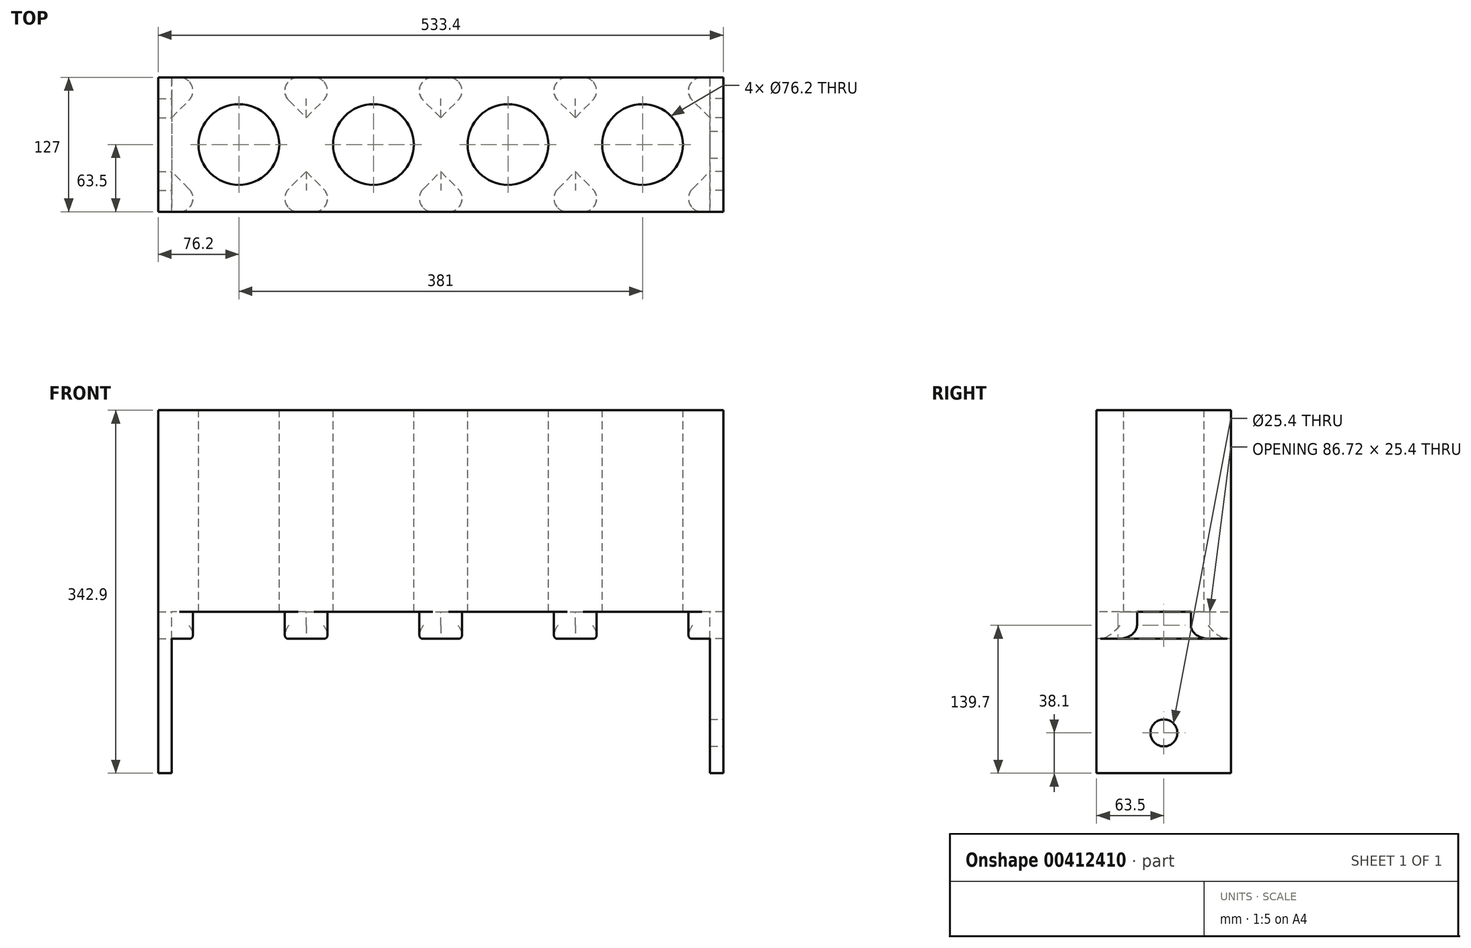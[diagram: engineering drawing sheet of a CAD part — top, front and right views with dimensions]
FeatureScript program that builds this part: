
annotation { "Feature Type Name" : "Feature", "Feature Type Description" : "" }
export const myFeature = defineFeature(function(context is Context, id is Id, definition is map)
    precondition{}
    {
        {
            var Q0;
            Q0=qCreatedBy(makeId("Top.planeOp"),FACE);
            var sketch = newSketch(context, id + "F0", { "sketchPlane" : qUnion([Q0])});
            skLineSegment(sketch, "E0", {"start": v(508, 0) * mm, "end": v(0, 0) * mm});
            skLineSegment(sketch, "E1", {"start": v(0, 0) * mm, "end": v(0, 127) * mm});
            skLineSegment(sketch, "E2", {"start": v(0, 127) * mm, "end": v(508, 127) * mm});
            skLineSegment(sketch, "E3", {"start": v(508, 0) * mm, "end": v(508, 127) * mm});
            skCircle(sketch, "E4", {"center": v(63.5, 63.5) * mm, "radius": 38.1 * mm});
            skCircle(sketch, "E5", {"center": v(190.5, 63.5) * mm, "radius": 38.1 * mm});
            skCircle(sketch, "E6", {"center": v(317.5, 63.5) * mm, "radius": 38.1 * mm});
            skCircle(sketch, "E7", {"center": v(444.5, 63.5) * mm, "radius": 38.1 * mm});
            skSolve(sketch);
        }
        {
            var Q0;
            Q0 = qSketchRegion(id + "F0", true);
            extrude(context, id + "F1", {"entities" : qUnion([Q0]), "oppositeDirection" : true, "depth" : 190.5 * mm});
        }
        {
            var Q0;
            Q0=makeQuery(id+"F1.opExtrude","CAP_FACE",FACE,{"disambiguationData":[OSD([sQuery(id+"F0.wireOp",EDGE,"E0"),sQuery(id+"F0.wireOp",EDGE,"E1"),sQuery(id+"F0.wireOp",EDGE,"E2"),sQuery(id+"F0.wireOp",EDGE,"E3"),sQuery(id+"F0.wireOp",EDGE,"E4"),sQuery(id+"F0.wireOp",EDGE,"E5"),sQuery(id+"F0.wireOp",EDGE,"E6"),sQuery(id+"F0.wireOp",EDGE,"E7")])],"isStart":false});
            var sketch = newSketch(context, id + "F2", { "sketchPlane" : qUnion([Q0])});
            skLineSegment(sketch, "E8", {"start": v(38.1, 0) * mm, "end": v(0, -38.1) * mm});
            skLineSegment(sketch, "E9", {"start": v(0, -88.9) * mm, "end": v(38.1, -127) * mm});
            skLineSegment(sketch, "E10", {"start": v(127, 0) * mm, "end": v(127, -38.1) * mm});
            skLineSegment(sketch, "E11", {"start": v(254, 0) * mm, "end": v(254, -127) * mm});
            skLineSegment(sketch, "E12", {"start": v(381, 0) * mm, "end": v(381, -127) * mm});
            skLineSegment(sketch, "E13", {"start": v(127, -38.1) * mm, "end": v(88.9, 0) * mm});
            skLineSegment(sketch, "E14", {"start": v(88.9, -127) * mm, "end": v(127, -88.9) * mm});
            skLineSegment(sketch, "E15", {"start": v(127, -38.1) * mm, "end": v(165.1, 0) * mm});
            skLineSegment(sketch, "E16", {"start": v(127, -88.9) * mm, "end": v(165.1, -127) * mm});
            skLineSegment(sketch, "E17", {"start": v(254, -88.9) * mm, "end": v(215.9, -127) * mm});
            skLineSegment(sketch, "E18", {"start": v(254, -88.9) * mm, "end": v(292.1, -127) * mm});
            skLineSegment(sketch, "E19", {"start": v(215.9, 0) * mm, "end": v(254, -38.1) * mm});
            skLineSegment(sketch, "E20", {"start": v(254, -38.1) * mm, "end": v(292.1, 0) * mm});
            skLineSegment(sketch, "E21", {"start": v(342.9, 0) * mm, "end": v(381, -38.1) * mm});
            skLineSegment(sketch, "E22", {"start": v(381, -38.1) * mm, "end": v(419.1, 0) * mm});
            skLineSegment(sketch, "E23", {"start": v(381, -88.9) * mm, "end": v(342.9, -127) * mm});
            skLineSegment(sketch, "E24", {"start": v(381, -88.9) * mm, "end": v(419.1, -127) * mm});
            skLineSegment(sketch, "E25", {"start": v(469.9, 0) * mm, "end": v(508, -38.1) * mm});
            skLineSegment(sketch, "E26", {"start": v(508, -88.9) * mm, "end": v(469.9, -127) * mm});
            skLineSegment(sketch, "E27.trimOffspring", {"start": v(127, -88.9) * mm, "end": v(127, -127) * mm});
            skSolve(sketch);
        }
        {
            var Q0;
            {var subQ3=sQuery(id+"F2.wireOp",EDGE,"E19");Q0=makeQuery(id+"F2.imprint","IMPRINT",FACE,{"disambiguationData":[TD([[makeQuery(id+"F2.imprint","IMPRINT",EDGE,{"derivedFrom":subQ3}),1.0]])]});}
            var Q1;
            {var subQ3=sQuery(id+"F2.wireOp",EDGE,"E20");Q1=makeQuery(id+"F2.imprint","IMPRINT",FACE,{"disambiguationData":[TD([[makeQuery(id+"F2.imprint","IMPRINT",EDGE,{"derivedFrom":subQ3}),1.0]])]});}
            var Q2;
            {var subQ3=sQuery(id+"F2.wireOp",EDGE,"E17");Q2=makeQuery(id+"F2.imprint","IMPRINT",FACE,{"disambiguationData":[TD([[makeQuery(id+"F2.imprint","IMPRINT",EDGE,{"derivedFrom":subQ3}),1.0]])]});}
            var Q3;
            {var subQ3=sQuery(id+"F2.wireOp",EDGE,"E18");Q3=makeQuery(id+"F2.imprint","IMPRINT",FACE,{"disambiguationData":[TD([[makeQuery(id+"F2.imprint","IMPRINT",EDGE,{"derivedFrom":subQ3}),-1.0]])]});}
            var Q4;
            {var subQ0=sQuery(id+"F2.wireOp",EDGE,"E10");Q4=makeQuery(id+"F2.imprint","IMPRINT",FACE,{"disambiguationData":[TD([[makeQuery(id+"F2.imprint","IMPRINT",EDGE,{"derivedFrom":subQ0}),1.0]])]});}
            var Q5;
            {var subQ0=sQuery(id+"F2.wireOp",EDGE,"E10");Q5=makeQuery(id+"F2.imprint","IMPRINT",FACE,{"disambiguationData":[TD([[makeQuery(id+"F2.imprint","IMPRINT",EDGE,{"derivedFrom":subQ0}),-1.0]])]});}
            var Q6;
            {var subQ0=sQuery(id+"F2.wireOp",EDGE,"E14");Q6=makeQuery(id+"F2.imprint","IMPRINT",FACE,{"disambiguationData":[TD([[makeQuery(id+"F2.imprint","IMPRINT",EDGE,{"derivedFrom":subQ0}),-1.0]])]});}
            var Q7;
            {var subQ0=sQuery(id+"F2.wireOp",EDGE,"E16");Q7=makeQuery(id+"F2.imprint","IMPRINT",FACE,{"disambiguationData":[TD([[makeQuery(id+"F2.imprint","IMPRINT",EDGE,{"derivedFrom":subQ0}),-1.0]])]});}
            var Q8;
            {var subQ0=sQuery(id+"F2.wireOp",EDGE,"E8");Q8=makeQuery(id+"F2.imprint","IMPRINT",FACE,{"disambiguationData":[TD([[makeQuery(id+"F2.imprint","IMPRINT",EDGE,{"derivedFrom":subQ0}),-1.0]])]});}
            var Q9;
            {var subQ0=sQuery(id+"F2.wireOp",EDGE,"E9");Q9=makeQuery(id+"F2.imprint","IMPRINT",FACE,{"disambiguationData":[TD([[makeQuery(id+"F2.imprint","IMPRINT",EDGE,{"derivedFrom":subQ0}),-1.0]])]});}
            var Q10;
            {var subQ3=sQuery(id+"F2.wireOp",EDGE,"E21");Q10=makeQuery(id+"F2.imprint","IMPRINT",FACE,{"disambiguationData":[TD([[makeQuery(id+"F2.imprint","IMPRINT",EDGE,{"derivedFrom":subQ3}),1.0]])]});}
            var Q11;
            {var subQ3=sQuery(id+"F2.wireOp",EDGE,"E22");Q11=makeQuery(id+"F2.imprint","IMPRINT",FACE,{"disambiguationData":[TD([[makeQuery(id+"F2.imprint","IMPRINT",EDGE,{"derivedFrom":subQ3}),1.0]])]});}
            var Q12;
            {var subQ0=sQuery(id+"F2.wireOp",EDGE,"E25");Q12=makeQuery(id+"F2.imprint","IMPRINT",FACE,{"disambiguationData":[TD([[makeQuery(id+"F2.imprint","IMPRINT",EDGE,{"derivedFrom":subQ0}),1.0]])]});}
            var Q13;
            {var subQ0=sQuery(id+"F2.wireOp",EDGE,"E26");Q13=makeQuery(id+"F2.imprint","IMPRINT",FACE,{"disambiguationData":[TD([[makeQuery(id+"F2.imprint","IMPRINT",EDGE,{"derivedFrom":subQ0}),1.0]])]});}
            var Q14;
            {var subQ3=sQuery(id+"F2.wireOp",EDGE,"E23");Q14=makeQuery(id+"F2.imprint","IMPRINT",FACE,{"disambiguationData":[TD([[makeQuery(id+"F2.imprint","IMPRINT",EDGE,{"derivedFrom":subQ3}),1.0]])]});}
            var Q15;
            {var subQ3=sQuery(id+"F2.wireOp",EDGE,"E24");Q15=makeQuery(id+"F2.imprint","IMPRINT",FACE,{"disambiguationData":[TD([[makeQuery(id+"F2.imprint","IMPRINT",EDGE,{"derivedFrom":subQ3}),-1.0]])]});}
            extrude(context, id + "F3", {"entities" : qUnion([Q0, Q1, Q2, Q3, Q4, Q5, Q6, Q7, Q8, Q9, Q10, Q11, Q12, Q13, Q14, Q15]), "operationType" : NewBodyOperationType.ADD, "depth" : 25.4 * mm});
        }
        {
            var Q0;
            Q0=makeQuery(id+"F3.opExtrude","CAP_EDGE",EDGE,{"disambiguationData":[OSD([sQuery(id+"F2.wireOp",EDGE,"E22")])],"isStart":false});
            var Q1;
            Q1=makeQuery(id+"F3.opExtrude","CAP_EDGE",EDGE,{"disambiguationData":[OSD([sQuery(id+"F2.wireOp",EDGE,"E21")])],"isStart":false});
            var Q2;
            Q2=makeQuery(id+"F3.opExtrude","CAP_EDGE",EDGE,{"disambiguationData":[OSD([sQuery(id+"F2.wireOp",EDGE,"E25")])],"isStart":false});
            var Q3;
            Q3=makeQuery(id+"F3.opExtrude","CAP_EDGE",EDGE,{"disambiguationData":[OSD([sQuery(id+"F2.wireOp",EDGE,"E26")])],"isStart":false});
            var Q4;
            Q4=makeQuery(id+"F3.opExtrude","CAP_EDGE",EDGE,{"disambiguationData":[OSD([sQuery(id+"F2.wireOp",EDGE,"E24")])],"isStart":false});
            var Q5;
            Q5=makeQuery(id+"F3.opExtrude","CAP_EDGE",EDGE,{"disambiguationData":[OSD([sQuery(id+"F2.wireOp",EDGE,"E23")])],"isStart":false});
            var Q6;
            Q6=makeQuery(id+"F3.opExtrude","CAP_EDGE",EDGE,{"disambiguationData":[OSD([sQuery(id+"F2.wireOp",EDGE,"E20")])],"isStart":false});
            var Q7;
            Q7=makeQuery(id+"F3.opExtrude","CAP_EDGE",EDGE,{"disambiguationData":[OSD([sQuery(id+"F2.wireOp",EDGE,"E18")])],"isStart":false});
            var Q8;
            Q8=makeQuery(id+"F3.opExtrude","CAP_EDGE",EDGE,{"disambiguationData":[OSD([sQuery(id+"F2.wireOp",EDGE,"E17")])],"isStart":false});
            var Q9;
            Q9=makeQuery(id+"F3.opExtrude","CAP_EDGE",EDGE,{"disambiguationData":[OSD([sQuery(id+"F2.wireOp",EDGE,"E19")])],"isStart":false});
            var Q10;
            Q10=makeQuery(id+"F3.opExtrude","CAP_EDGE",EDGE,{"disambiguationData":[OSD([sQuery(id+"F2.wireOp",EDGE,"E15")])],"isStart":false});
            var Q11;
            Q11=makeQuery(id+"F3.opExtrude","CAP_EDGE",EDGE,{"disambiguationData":[OSD([sQuery(id+"F2.wireOp",EDGE,"E13")])],"isStart":false});
            var Q12;
            Q12=makeQuery(id+"F3.opExtrude","CAP_EDGE",EDGE,{"disambiguationData":[OSD([sQuery(id+"F2.wireOp",EDGE,"E14")])],"isStart":false});
            var Q13;
            Q13=makeQuery(id+"F3.opExtrude","CAP_EDGE",EDGE,{"disambiguationData":[OSD([sQuery(id+"F2.wireOp",EDGE,"E16")])],"isStart":false});
            var Q14;
            Q14=makeQuery(id+"F3.opExtrude","CAP_EDGE",EDGE,{"disambiguationData":[OSD([sQuery(id+"F2.wireOp",EDGE,"E8")])],"isStart":false});
            var Q15;
            Q15=makeQuery(id+"F3.opExtrude","CAP_EDGE",EDGE,{"disambiguationData":[OSD([sQuery(id+"F2.wireOp",EDGE,"E9")])],"isStart":false});
            var Q16;
            Q16=makeQuery(id+"F3.opExtrude","SWEPT_EDGE",EDGE,{"disambiguationData":[OSD([sQuery(id+"F0.wireOp",EDGE,"E0"),sQuery(id+"F2.wireOp",EDGE,"E20")])]});
            var Q17;
            Q17=makeQuery(id+"F3.opExtrude","SWEPT_EDGE",EDGE,{"disambiguationData":[OSD([sQuery(id+"F0.wireOp",EDGE,"E0"),sQuery(id+"F2.wireOp",EDGE,"E19")])]});
            var Q18;
            Q18=makeQuery(id+"F3.opExtrude","SWEPT_EDGE",EDGE,{"disambiguationData":[OSD([sQuery(id+"F0.wireOp",EDGE,"E2"),sQuery(id+"F2.wireOp",EDGE,"E18")])]});
            var Q19;
            Q19=makeQuery(id+"F3.opExtrude","SWEPT_EDGE",EDGE,{"disambiguationData":[OSD([sQuery(id+"F0.wireOp",EDGE,"E2"),sQuery(id+"F2.wireOp",EDGE,"E17")])]});
            var Q20;
            Q20=makeQuery(id+"F3.opExtrude","SWEPT_EDGE",EDGE,{"disambiguationData":[OSD([sQuery(id+"F0.wireOp",EDGE,"E2"),sQuery(id+"F2.wireOp",EDGE,"E23")])]});
            var Q21;
            Q21=makeQuery(id+"F3.opExtrude","SWEPT_EDGE",EDGE,{"disambiguationData":[OSD([sQuery(id+"F0.wireOp",EDGE,"E2"),sQuery(id+"F2.wireOp",EDGE,"E24")])]});
            var Q22;
            Q22=makeQuery(id+"F3.opExtrude","SWEPT_EDGE",EDGE,{"disambiguationData":[OSD([sQuery(id+"F0.wireOp",EDGE,"E2"),sQuery(id+"F2.wireOp",EDGE,"E26")])]});
            var Q23;
            Q23=makeQuery(id+"F3.opExtrude","SWEPT_EDGE",EDGE,{"disambiguationData":[OSD([sQuery(id+"F0.wireOp",EDGE,"E0"),sQuery(id+"F2.wireOp",EDGE,"E25")])]});
            var Q24;
            Q24=makeQuery(id+"F3.opExtrude","SWEPT_EDGE",EDGE,{"disambiguationData":[OSD([sQuery(id+"F0.wireOp",EDGE,"E0"),sQuery(id+"F2.wireOp",EDGE,"E22")])]});
            var Q25;
            Q25=makeQuery(id+"F3.opExtrude","SWEPT_EDGE",EDGE,{"disambiguationData":[OSD([sQuery(id+"F0.wireOp",EDGE,"E0"),sQuery(id+"F2.wireOp",EDGE,"E21")])]});
            var Q26;
            Q26=makeQuery(id+"F3.opExtrude","SWEPT_EDGE",EDGE,{"disambiguationData":[OSD([sQuery(id+"F0.wireOp",EDGE,"E0"),sQuery(id+"F2.wireOp",EDGE,"E13")])]});
            var Q27;
            Q27=makeQuery(id+"F3.opExtrude","SWEPT_EDGE",EDGE,{"disambiguationData":[OSD([sQuery(id+"F0.wireOp",EDGE,"E0"),sQuery(id+"F2.wireOp",EDGE,"E15")])]});
            var Q28;
            Q28=makeQuery(id+"F3.opExtrude","SWEPT_EDGE",EDGE,{"disambiguationData":[OSD([sQuery(id+"F0.wireOp",EDGE,"E2"),sQuery(id+"F2.wireOp",EDGE,"E14")])]});
            var Q29;
            Q29=makeQuery(id+"F3.opExtrude","SWEPT_EDGE",EDGE,{"disambiguationData":[OSD([sQuery(id+"F0.wireOp",EDGE,"E2"),sQuery(id+"F2.wireOp",EDGE,"E16")])]});
            var Q30;
            Q30=makeQuery(id+"F3.opExtrude","SWEPT_EDGE",EDGE,{"disambiguationData":[OSD([sQuery(id+"F0.wireOp",EDGE,"E2"),sQuery(id+"F2.wireOp",EDGE,"E9")])]});
            var Q31;
            Q31=makeQuery(id+"F3.opExtrude","SWEPT_EDGE",EDGE,{"disambiguationData":[OSD([sQuery(id+"F0.wireOp",EDGE,"E0"),sQuery(id+"F2.wireOp",EDGE,"E8")])]});
            fillet(context, id + "F4", {"entities" : qUnion([Q0, Q1, Q2, Q3, Q4, Q5, Q6, Q7, Q8, Q9, Q10, Q11, Q12, Q13, Q14, Q15, Q16, Q17, Q18, Q19, Q20, Q21, Q22, Q23, Q24, Q25, Q26, Q27, Q28, Q29, Q30, Q31]), "radius" : 12.7 * mm, "tangentPropagation" : true, "allowEdgeOverflow" : false});
        }
        {
            var Q0;
            {var subQ0=sQuery(id+"F0.wireOp",EDGE,"E3");var subQ1=makeQuery(id+"F1.opExtrude","CAP_EDGE",EDGE,{"disambiguationData":[OSD([subQ0])],"isStart":false});Q0=makeQuery(id+"F3.boolean.opBoolean","MERGE",FACE,{"derivedFrom":[makeQuery(id+"F1.opExtrude","SWEPT_FACE",FACE,{"disambiguationData":[OSD([subQ0])]}),makeQuery(id+"F3.opExtrude","SWEPT_FACE",FACE,{"disambiguationData":[OSD([subQ0]),TDD([makeQuery(id+"F2.imprint","IMPRINT",EDGE,{"disambiguationData":[TD([[makeQuery(id+"F2.imprint","INTERSECT",VERTEX,{"derivedFrom":[makeQuery(id+"F1.opExtrude","CAP_EDGE",EDGE,{"disambiguationData":[OSD([sQuery(id+"F0.wireOp",EDGE,"E0")])],"isStart":false}),subQ1]}),-1.0]])],"derivedFrom":subQ1})])]}),makeQuery(id+"F3.opExtrude","SWEPT_FACE",FACE,{"disambiguationData":[OSD([subQ0]),TDD([makeQuery(id+"F2.imprint","IMPRINT",EDGE,{"disambiguationData":[TD([[makeQuery(id+"F2.imprint","INTERSECT",VERTEX,{"derivedFrom":[makeQuery(id+"F1.opExtrude","CAP_EDGE",EDGE,{"disambiguationData":[OSD([sQuery(id+"F0.wireOp",EDGE,"E2")])],"isStart":false}),subQ1]}),1.0]])],"derivedFrom":subQ1})])]})]});}
            var sketch = newSketch(context, id + "F5", { "sketchPlane" : qUnion([Q0])});
            skLineSegment(sketch, "E28", {"start": v(127, -342.9) * mm, "end": v(127, -215.9) * mm});
            skLineSegment(sketch, "E29", {"start": v(127, -342.9) * mm, "end": v(0, -342.9) * mm});
            skLineSegment(sketch, "E30", {"start": v(0, -342.9) * mm, "end": v(0, -215.9) * mm});
            skLineSegment(sketch, "E31", {"start": v(0, -215.9) * mm, "end": v(127, -215.9) * mm});
            skSolve(sketch);
        }
        {
            var Q0;
            Q0 = qSketchRegion(id + "F5", true);
            var Q1;
            {var subQ0=sQuery(id+"F0.wireOp",EDGE,"E3");Q1=makeQuery(id+"F5.imprint","IMPRINT",FACE,{"disambiguationData":[TD([[makeQuery(id+"F5.imprint","IMPRINT",EDGE,{"derivedFrom":makeQuery(id+"F1.opExtrude","CAP_EDGE",EDGE,{"disambiguationData":[OSD([subQ0])],"isStart":true})}),-1.0]])]});}
            extrude(context, id + "F6", {"entities" : qUnion([Q0, Q1]), "operationType" : NewBodyOperationType.ADD, "depth" : 12.7 * mm});
        }
        {
            var Q0;
            {var subQ0=sQuery(id+"F0.wireOp",EDGE,"E1");var subQ1=makeQuery(id+"F1.opExtrude","CAP_EDGE",EDGE,{"disambiguationData":[OSD([subQ0])],"isStart":false});Q0=makeQuery(id+"F3.boolean.opBoolean","MERGE",FACE,{"derivedFrom":[makeQuery(id+"F1.opExtrude","SWEPT_FACE",FACE,{"disambiguationData":[OSD([subQ0])]}),makeQuery(id+"F3.opExtrude","SWEPT_FACE",FACE,{"disambiguationData":[OSD([subQ0]),TDD([makeQuery(id+"F2.imprint","IMPRINT",EDGE,{"disambiguationData":[TD([[makeQuery(id+"F2.imprint","INTERSECT",VERTEX,{"derivedFrom":[makeQuery(id+"F1.opExtrude","CAP_EDGE",EDGE,{"disambiguationData":[OSD([sQuery(id+"F0.wireOp",EDGE,"E0")])],"isStart":false}),subQ1]}),-1.0]])],"derivedFrom":subQ1})])]}),makeQuery(id+"F3.opExtrude","SWEPT_FACE",FACE,{"disambiguationData":[OSD([subQ0]),TDD([makeQuery(id+"F2.imprint","IMPRINT",EDGE,{"disambiguationData":[TD([[makeQuery(id+"F2.imprint","INTERSECT",VERTEX,{"derivedFrom":[subQ1,makeQuery(id+"F1.opExtrude","CAP_EDGE",EDGE,{"disambiguationData":[OSD([sQuery(id+"F0.wireOp",EDGE,"E2")])],"isStart":false})]}),1.0]])],"derivedFrom":subQ1})])]})]});}
            var sketch = newSketch(context, id + "F7", { "sketchPlane" : qUnion([Q0])});
            skLineSegment(sketch, "E32", {"start": v(0, -215.9) * mm, "end": v(0, -342.9) * mm});
            skLineSegment(sketch, "E33", {"start": v(-127, -215.9) * mm, "end": v(-127, -342.9) * mm});
            skLineSegment(sketch, "E34", {"start": v(-127, -342.9) * mm, "end": v(0, -342.9) * mm});
            skLineSegment(sketch, "E35", {"start": v(-127, -215.9) * mm, "end": v(0, -215.9) * mm});
            skSolve(sketch);
        }
        {
            var Q0;
            Q0 = qSketchRegion(id + "F7", true);
            var Q1;
            {var subQ0=sQuery(id+"F0.wireOp",EDGE,"E1");Q1=makeQuery(id+"F7.imprint","IMPRINT",FACE,{"disambiguationData":[TD([[makeQuery(id+"F7.imprint","IMPRINT",EDGE,{"derivedFrom":makeQuery(id+"F1.opExtrude","CAP_EDGE",EDGE,{"disambiguationData":[OSD([subQ0])],"isStart":true})}),1.0]])]});}
            extrude(context, id + "F8", {"entities" : qUnion([Q0, Q1]), "operationType" : NewBodyOperationType.ADD, "depth" : 12.7 * mm});
        }
        {
            var Q0;
            Q0=makeQuery(id+"F6.opExtrude","CAP_FACE",FACE,{"disambiguationData":[OSD([sQuery(id+"F0.wireOp",EDGE,"E0"),sQuery(id+"F0.wireOp",EDGE,"E2"),sQuery(id+"F0.wireOp",EDGE,"E3"),sQuery(id+"F2.wireOp",EDGE,"E25"),sQuery(id+"F2.wireOp",EDGE,"E26"),sQuery(id+"F5.wireOp",EDGE,"E28"),sQuery(id+"F5.wireOp",EDGE,"E29"),sQuery(id+"F5.wireOp",EDGE,"E30"),sQuery(id+"F5.wireOp",EDGE,"E31")])],"isStart":false});
            var sketch = newSketch(context, id + "F9", { "sketchPlane" : qUnion([Q0])});
            skCircle(sketch, "E36", {"center": v(63.5, -304.8) * mm, "radius": 12.7 * mm});
            skPoint(sketch, "E36.centerSnap0", {"position": v(63.5, -342.9) * mm});
            skSolve(sketch);
        }
        {
            var Q0;
            Q0 = qSketchRegion(id + "F9", true);
            extrude(context, id + "F10", {"entities" : qUnion([Q0]), "operationType" : NewBodyOperationType.REMOVE, "oppositeDirection" : true, "depth" : 25.4 * mm});
        }
    });
